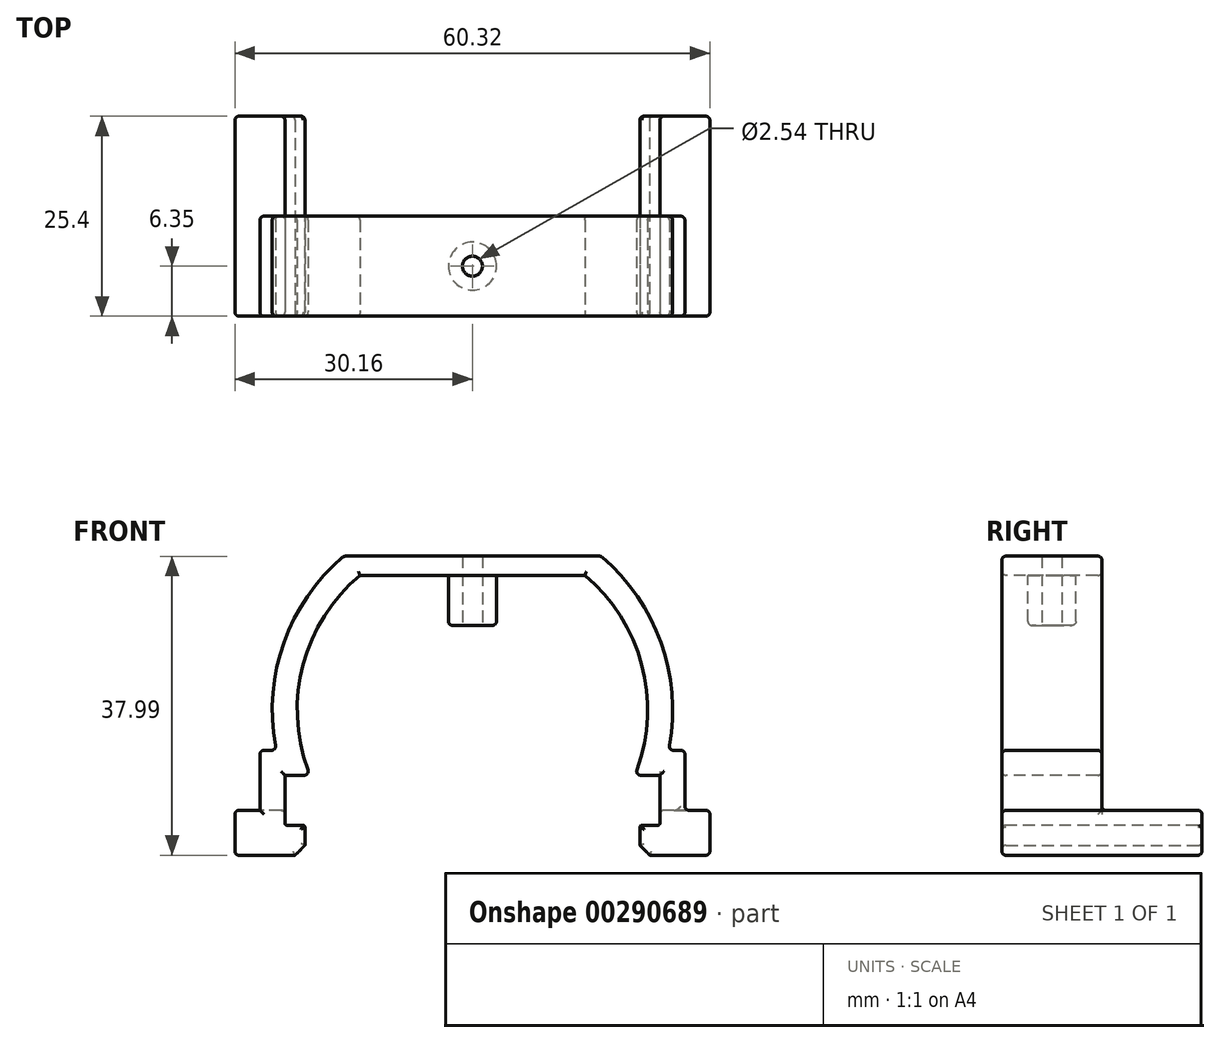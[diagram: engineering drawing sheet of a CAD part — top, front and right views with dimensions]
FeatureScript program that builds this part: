
annotation { "Feature Type Name" : "Feature", "Feature Type Description" : "" }
export const myFeature = defineFeature(function(context is Context, id is Id, definition is map)
    precondition{}
    {
        {
            var Q0;
            Q0=qCreatedBy(makeId("Front.planeOp"),FACE);
            var sketch = newSketch(context, id + "F0", { "sketchPlane" : qUnion([Q0])});
            skLineSegment(sketch, "E0", {"start": v(-23.81, 0) * mm, "end": v(-20.64, 0) * mm});
            skLineSegment(sketch, "E1", {"start": v(0, 0) * mm, "end": v(0, 25.4) * mm, "construction": true});
            skLineSegment(sketch, "E2", {"start": v(-14.29, 25.4) * mm, "end": v(14.29, 25.4) * mm});
            skLineSegment(sketch, "E3", {"start": v(-23.81, 0) * mm, "end": v(-20.64, 0) * mm, "construction": true});
            skLineSegment(sketch, "E4", {"start": v(23.81, 0) * mm, "end": v(20.64, 0) * mm, "construction": true});
            skArc(sketch, "E5", {"start": v(-14.29, 25.4) * mm, "mid": v(-21.6, 13.73) * mm, "end": v(-20.64, 0) * mm});
            skLineSegment(sketch, "E6", {"start": v(-23.81, 0) * mm, "end": v(-23.81, -6.35) * mm});
            skLineSegment(sketch, "E7", {"start": v(23.81, 0) * mm, "end": v(23.81, -6.35) * mm});
            skArc(sketch, "E8.0", {"start": v(-16.33, 27.83) * mm, "mid": v(-24.02, 16.69) * mm, "end": v(-24.9, 3.18) * mm});
            skLineSegment(sketch, "E9", {"start": v(-16.33, 27.83) * mm, "end": v(16.33, 27.83) * mm});
            skLineSegment(sketch, "E10", {"start": v(-26.99, -4.45) * mm, "end": v(-26.99, 3.17) * mm});
            skLineSegment(sketch, "E11", {"start": v(-26.99, 3.17) * mm, "end": v(-24.9, 3.17) * mm});
            skLineSegment(sketch, "E12", {"start": v(26.99, -4.45) * mm, "end": v(26.99, 3.18) * mm});
            skLineSegment(sketch, "E13", {"start": v(26.99, 3.18) * mm, "end": v(24.9, 3.18) * mm});
            skArc(sketch, "E14.trimOffspring", {"start": v(24.9, 3.18) * mm, "mid": v(24.02, 16.69) * mm, "end": v(16.33, 27.83) * mm});
            skArc(sketch, "E15.trimOffspring", {"start": v(20.64, 0) * mm, "mid": v(21.6, 13.73) * mm, "end": v(14.29, 25.4) * mm});
            skLineSegment(sketch, "E16.trimOffspring", {"start": v(20.64, 0) * mm, "end": v(23.81, 0) * mm});
            skLineSegment(sketch, "E17", {"start": v(-23.81, -6.35) * mm, "end": v(-21.27, -6.35) * mm});
            skLineSegment(sketch, "E18", {"start": v(23.81, -6.35) * mm, "end": v(21.27, -6.35) * mm});
            skLineSegment(sketch, "E19", {"start": v(-26.99, -4.45) * mm, "end": v(-30.16, -4.45) * mm});
            skLineSegment(sketch, "E20", {"start": v(26.99, -4.45) * mm, "end": v(30.16, -4.45) * mm});
            skLineSegment(sketch, "E21", {"start": v(-30.16, -4.45) * mm, "end": v(-30.16, -10.16) * mm});
            skLineSegment(sketch, "E22", {"start": v(30.16, -4.45) * mm, "end": v(30.16, -10.16) * mm});
            skLineSegment(sketch, "E23", {"start": v(-21.27, -6.35) * mm, "end": v(-21.27, -10.16) * mm});
            skLineSegment(sketch, "E24", {"start": v(21.27, -6.35) * mm, "end": v(21.27, -10.16) * mm});
            skLineSegment(sketch, "E25", {"start": v(-21.27, -10.16) * mm, "end": v(-30.16, -10.16) * mm});
            skLineSegment(sketch, "E26", {"start": v(21.27, -10.16) * mm, "end": v(30.16, -10.16) * mm});
            skSolve(sketch);
        }
        {
            var Q0;
            Q0=makeQuery(id+"F0.imprint","IMPRINT",FACE,{"disambiguationData":[TD([[makeQuery(id+"F0.imprint","IMPRINT",EDGE,{"derivedFrom":sQuery(id+"F0.wireOp",EDGE,"E0")}),1.0]])]});
            extrude(context, id + "F1", {"entities" : qUnion([Q0]), "oppositeDirection" : true, "depth" : 12.7 * mm});
        }
        {
            var Q0;
            Q0=makeQuery(id+"F1.opExtrude","SWEPT_FACE",FACE,{"disambiguationData":[OSD([sQuery(id+"F0.wireOp",EDGE,"E2")])]});
            var sketch = newSketch(context, id + "F2", { "sketchPlane" : qUnion([Q0])});
            skLineSegment(sketch, "E27", {"start": v(0, -12.7) * mm, "end": v(0, -6.35) * mm, "construction": true});
            skPoint(sketch, "E27.endSnap0", {"position": v(0, -12.7) * mm});
            skCircle(sketch, "E28", {"center": v(0, -6.35) * mm, "radius": 3.05 * mm});
            skSolve(sketch);
        }
        {
            var Q0;
            Q0=makeQuery(id+"F2.imprint","IMPRINT",FACE,{"disambiguationData":[TD([[makeQuery(id+"F2.imprint","IMPRINT",EDGE,{"derivedFrom":sQuery(id+"F2.wireOp",EDGE,"E28")}),1.0]])]});
            extrude(context, id + "F3", {"entities" : qUnion([Q0]), "operationType" : NewBodyOperationType.ADD, "depth" : 6.35 * mm});
        }
        {
            var Q0;
            Q0=makeQuery(id+"F1.opExtrude","SWEPT_EDGE",EDGE,{"disambiguationData":[OSD([sQuery(id+"F0.wireOp",EDGE,"E17"),sQuery(id+"F0.wireOp",EDGE,"sQ2Dt9HJ-DLmy-fobY-wEzB-knzwlTL04auf")])]});
            var Q1;
            Q1=makeQuery(id+"F1.opExtrude","SWEPT_EDGE",EDGE,{"disambiguationData":[OSD([sQuery(id+"F0.wireOp",EDGE,"E18"),sQuery(id+"F0.wireOp",EDGE,"bWk3n836-9KEs-FhVF-pOS5-eo05tRzIyBKB")])]});
            fillet(context, id + "F4", {"entities" : qUnion([Q0, Q1]), "radius" : 0.25 * mm, "tangentPropagation" : true, "allowEdgeOverflow" : false});
        }
        {
            var Q0;
            Q0=makeQuery(id+"F1.opExtrude","SWEPT_EDGE",EDGE,{"disambiguationData":[OSD([sQuery(id+"F0.wireOp",EDGE,"E24"),sQuery(id+"F0.wireOp",EDGE,"E26")])]});
            chamfer(context, id + "F5", {"entities" : qUnion([Q0]), "width" : 1.27 * mm, "tangentPropagation" : true});
        }
        {
            var Q0;
            Q0=makeQuery(id+"F1.opExtrude","CAP_FACE",FACE,{"disambiguationData":[OSD([sQuery(id+"F0.wireOp",EDGE,"E0"),sQuery(id+"F0.wireOp",EDGE,"E2"),sQuery(id+"F0.wireOp",EDGE,"E5"),sQuery(id+"F0.wireOp",EDGE,"E6"),sQuery(id+"F0.wireOp",EDGE,"E7"),sQuery(id+"F0.wireOp",EDGE,"E8.0"),sQuery(id+"F0.wireOp",EDGE,"E9"),sQuery(id+"F0.wireOp",EDGE,"E10"),sQuery(id+"F0.wireOp",EDGE,"E11"),sQuery(id+"F0.wireOp",EDGE,"E12"),sQuery(id+"F0.wireOp",EDGE,"E13"),sQuery(id+"F0.wireOp",EDGE,"E14.trimOffspring"),sQuery(id+"F0.wireOp",EDGE,"E15.trimOffspring"),sQuery(id+"F0.wireOp",EDGE,"E16.trimOffspring"),sQuery(id+"F0.wireOp",EDGE,"E17"),sQuery(id+"F0.wireOp",EDGE,"E18"),sQuery(id+"F0.wireOp",EDGE,"E19"),sQuery(id+"F0.wireOp",EDGE,"E20"),sQuery(id+"F0.wireOp",EDGE,"E21"),sQuery(id+"F0.wireOp",EDGE,"E22"),sQuery(id+"F0.wireOp",EDGE,"E23"),sQuery(id+"F0.wireOp",EDGE,"E24"),sQuery(id+"F0.wireOp",EDGE,"E25"),sQuery(id+"F0.wireOp",EDGE,"E26")])],"isStart":false});
            var sketch = newSketch(context, id + "F6", { "sketchPlane" : qUnion([Q0])});
            skLineSegment(sketch, "E29", {"start": v(-26.99, -4.45) * mm, "end": v(-23.81, -4.45) * mm});
            skSolve(sketch);
        }
        {
            var Q0;
            {var subQ3=sQuery(id+"F6.wireOp",EDGE,"E29");Q0=makeQuery(id+"F6.imprint","IMPRINT",FACE,{"disambiguationData":[TD([[makeQuery(id+"F6.imprint","IMPRINT",EDGE,{"derivedFrom":subQ3}),-1.0]])]});}
            extrude(context, id + "F7", {"entities" : qUnion([Q0]), "operationType" : NewBodyOperationType.ADD, "depth" : 12.7 * mm});
        }
        {
            var Q0;
            Q0=makeQuery(id+"F1.opExtrude","CAP_FACE",FACE,{"disambiguationData":[OSD([sQuery(id+"F0.wireOp",EDGE,"E0"),sQuery(id+"F0.wireOp",EDGE,"E2"),sQuery(id+"F0.wireOp",EDGE,"E5"),sQuery(id+"F0.wireOp",EDGE,"E6"),sQuery(id+"F0.wireOp",EDGE,"E7"),sQuery(id+"F0.wireOp",EDGE,"E8.0"),sQuery(id+"F0.wireOp",EDGE,"E9"),sQuery(id+"F0.wireOp",EDGE,"E10"),sQuery(id+"F0.wireOp",EDGE,"E11"),sQuery(id+"F0.wireOp",EDGE,"E12"),sQuery(id+"F0.wireOp",EDGE,"E13"),sQuery(id+"F0.wireOp",EDGE,"E14.trimOffspring"),sQuery(id+"F0.wireOp",EDGE,"E15.trimOffspring"),sQuery(id+"F0.wireOp",EDGE,"E16.trimOffspring"),sQuery(id+"F0.wireOp",EDGE,"E17"),sQuery(id+"F0.wireOp",EDGE,"E18"),sQuery(id+"F0.wireOp",EDGE,"E19"),sQuery(id+"F0.wireOp",EDGE,"E20"),sQuery(id+"F0.wireOp",EDGE,"E21"),sQuery(id+"F0.wireOp",EDGE,"E22"),sQuery(id+"F0.wireOp",EDGE,"E23"),sQuery(id+"F0.wireOp",EDGE,"E24"),sQuery(id+"F0.wireOp",EDGE,"E25"),sQuery(id+"F0.wireOp",EDGE,"E26")])],"isStart":false});
            var sketch = newSketch(context, id + "F8", { "sketchPlane" : qUnion([Q0])});
            skLineSegment(sketch, "E30", {"start": v(26.99, -4.45) * mm, "end": v(23.81, -4.45) * mm});
            skSolve(sketch);
        }
        {
            var Q0;
            {var subQ9=sQuery(id+"F8.wireOp",EDGE,"E30");Q0=makeQuery(id+"F8.imprint","IMPRINT",FACE,{"disambiguationData":[TD([[makeQuery(id+"F8.imprint","IMPRINT",EDGE,{"derivedFrom":subQ9}),1.0]])]});}
            extrude(context, id + "F9", {"entities" : qUnion([Q0]), "operationType" : NewBodyOperationType.ADD, "depth" : 12.7 * mm});
        }
        {
            var Q0;
            {var subQ0=sQuery(id+"F0.wireOp",EDGE,"E25");var subQ1=sQuery(id+"F0.wireOp",EDGE,"E23");Q0=makeQuery(id+"F9.boolean.opBoolean","MERGE",EDGE,{"derivedFrom":[makeQuery(id+"F1.opExtrude","SWEPT_EDGE",EDGE,{"disambiguationData":[OSD([subQ1,subQ0])]}),makeQuery(id+"F9.opExtrude","SWEPT_EDGE",EDGE,{"disambiguationData":[OSD([subQ1,subQ0])]})]});}
            chamfer(context, id + "F10", {"entities" : qUnion([Q0]), "width" : 1.27 * mm, "tangentPropagation" : true});
        }
        {
            var Q0;
            Q0=makeQuery(id+"F1.opExtrude","CAP_EDGE",EDGE,{"disambiguationData":[OSD([sQuery(id+"F0.wireOp",EDGE,"E5")])],"isStart":true});
            var Q1;
            Q1=makeQuery(id+"F1.opExtrude","SWEPT_EDGE",EDGE,{"disambiguationData":[OSD([sQuery(id+"F0.wireOp",EDGE,"E0"),sQuery(id+"F0.wireOp",EDGE,"E5")])]});
            var Q2;
            Q2=makeQuery(id+"F1.opExtrude","CAP_EDGE",EDGE,{"disambiguationData":[OSD([sQuery(id+"F0.wireOp",EDGE,"E5")])],"isStart":false});
            var Q3;
            Q3=makeQuery(id+"F1.opExtrude","SWEPT_EDGE",EDGE,{"disambiguationData":[OSD([sQuery(id+"F0.wireOp",EDGE,"E13"),sQuery(id+"F0.wireOp",EDGE,"E14.trimOffspring")])]});
            var Q4;
            Q4=makeQuery(id+"F1.opExtrude","CAP_EDGE",EDGE,{"disambiguationData":[OSD([sQuery(id+"F0.wireOp",EDGE,"E6")])],"isStart":true});
            var Q5;
            Q5=makeQuery(id+"F1.opExtrude","CAP_EDGE",EDGE,{"disambiguationData":[OSD([sQuery(id+"F0.wireOp",EDGE,"E0")])],"isStart":true});
            var Q6;
            Q6=makeQuery(id+"F1.opExtrude","CAP_EDGE",EDGE,{"disambiguationData":[OSD([sQuery(id+"F0.wireOp",EDGE,"E17")])],"isStart":true});
            var Q7;
            Q7=makeQuery(id+"F1.opExtrude","CAP_EDGE",EDGE,{"disambiguationData":[OSD([sQuery(id+"F0.wireOp",EDGE,"E22")])],"isStart":true});
            var Q8;
            Q8=makeQuery(id+"F1.opExtrude","CAP_EDGE",EDGE,{"disambiguationData":[OSD([sQuery(id+"F0.wireOp",EDGE,"E18")])],"isStart":true});
            var Q9;
            Q9=makeQuery(id+"F1.opExtrude","CAP_EDGE",EDGE,{"disambiguationData":[OSD([sQuery(id+"F0.wireOp",EDGE,"E12")])],"isStart":true});
            var Q10;
            Q10=makeQuery(id+"F1.opExtrude","CAP_EDGE",EDGE,{"disambiguationData":[OSD([sQuery(id+"F0.wireOp",EDGE,"E14.trimOffspring")])],"isStart":true});
            var Q11;
            Q11=makeQuery(id+"F1.opExtrude","CAP_EDGE",EDGE,{"disambiguationData":[OSD([sQuery(id+"F0.wireOp",EDGE,"E13")])],"isStart":true});
            var Q12;
            Q12=makeQuery(id+"F1.opExtrude","CAP_EDGE",EDGE,{"disambiguationData":[OSD([sQuery(id+"F0.wireOp",EDGE,"E13")])],"isStart":false});
            var Q13;
            Q13=makeQuery(id+"F1.opExtrude","CAP_EDGE",EDGE,{"disambiguationData":[OSD([sQuery(id+"F0.wireOp",EDGE,"E20")])],"isStart":true});
            var Q14;
            Q14=makeQuery(id+"F1.opExtrude","CAP_EDGE",EDGE,{"disambiguationData":[OSD([sQuery(id+"F0.wireOp",EDGE,"E16.trimOffspring")])],"isStart":false});
            var Q15;
            Q15=makeQuery(id+"F1.opExtrude","SWEPT_EDGE",EDGE,{"disambiguationData":[OSD([sQuery(id+"F0.wireOp",EDGE,"E15.trimOffspring"),sQuery(id+"F0.wireOp",EDGE,"E16.trimOffspring")])]});
            var Q16;
            Q16=makeQuery(id+"F1.opExtrude","CAP_EDGE",EDGE,{"disambiguationData":[OSD([sQuery(id+"F0.wireOp",EDGE,"E9")])],"isStart":false});
            var Q17;
            Q17=makeQuery(id+"F1.opExtrude","CAP_EDGE",EDGE,{"disambiguationData":[OSD([sQuery(id+"F0.wireOp",EDGE,"E2")])],"isStart":false});
            var Q18;
            Q18=makeQuery(id+"F1.opExtrude","CAP_EDGE",EDGE,{"disambiguationData":[OSD([sQuery(id+"F0.wireOp",EDGE,"E15.trimOffspring")])],"isStart":false});
            var Q19;
            Q19=makeQuery(id+"F1.opExtrude","CAP_EDGE",EDGE,{"disambiguationData":[OSD([sQuery(id+"F0.wireOp",EDGE,"E14.trimOffspring")])],"isStart":false});
            var Q20;
            Q20=makeQuery(id+"F1.opExtrude","SWEPT_EDGE",EDGE,{"disambiguationData":[OSD([sQuery(id+"F0.wireOp",EDGE,"E9"),sQuery(id+"F0.wireOp",EDGE,"E14.trimOffspring")])]});
            var Q21;
            Q21=makeQuery(id+"F1.opExtrude","SWEPT_EDGE",EDGE,{"disambiguationData":[OSD([sQuery(id+"F0.wireOp",EDGE,"E8.0"),sQuery(id+"F0.wireOp",EDGE,"E9")])]});
            var Q22;
            Q22=makeQuery(id+"F1.opExtrude","CAP_EDGE",EDGE,{"disambiguationData":[OSD([sQuery(id+"F0.wireOp",EDGE,"E9")])],"isStart":true});
            var Q23;
            Q23=makeQuery(id+"F1.opExtrude","CAP_EDGE",EDGE,{"disambiguationData":[OSD([sQuery(id+"F0.wireOp",EDGE,"E8.0")])],"isStart":true});
            var Q24;
            Q24=makeQuery(id+"F1.opExtrude","SWEPT_EDGE",EDGE,{"disambiguationData":[OSD([sQuery(id+"F0.wireOp",EDGE,"E8.0"),sQuery(id+"F0.wireOp",EDGE,"E11")])]});
            var Q25;
            Q25=makeQuery(id+"F1.opExtrude","CAP_EDGE",EDGE,{"disambiguationData":[OSD([sQuery(id+"F0.wireOp",EDGE,"E0")])],"isStart":false});
            var Q26;
            Q26=makeQuery(id+"F1.opExtrude","CAP_EDGE",EDGE,{"disambiguationData":[OSD([sQuery(id+"F0.wireOp",EDGE,"E8.0")])],"isStart":false});
            var Q27;
            Q27=makeQuery(id+"F1.opExtrude","CAP_EDGE",EDGE,{"disambiguationData":[OSD([sQuery(id+"F0.wireOp",EDGE,"E11")])],"isStart":false});
            var Q28;
            Q28=makeQuery(id+"F1.opExtrude","CAP_EDGE",EDGE,{"disambiguationData":[OSD([sQuery(id+"F0.wireOp",EDGE,"E10")])],"isStart":true});
            var Q29;
            Q29=makeQuery(id+"F1.opExtrude","CAP_EDGE",EDGE,{"disambiguationData":[OSD([sQuery(id+"F0.wireOp",EDGE,"E11")])],"isStart":true});
            var Q30;
            Q30=makeQuery(id+"F1.opExtrude","SWEPT_EDGE",EDGE,{"disambiguationData":[OSD([sQuery(id+"F0.wireOp",EDGE,"E19"),sQuery(id+"F0.wireOp",EDGE,"E21")])]});
            var Q31;
            Q31=makeQuery(id+"F1.opExtrude","CAP_EDGE",EDGE,{"disambiguationData":[OSD([sQuery(id+"F0.wireOp",EDGE,"E19")])],"isStart":true});
            var Q32;
            Q32=makeQuery(id+"F1.opExtrude","CAP_EDGE",EDGE,{"disambiguationData":[OSD([sQuery(id+"F0.wireOp",EDGE,"E21")])],"isStart":true});
            var Q33;
            Q33=makeQuery(id+"F1.opExtrude","SWEPT_EDGE",EDGE,{"disambiguationData":[OSD([sQuery(id+"F0.wireOp",EDGE,"E19"),sQuery(id+"F0.wireOp",EDGE,"E21")])]});
            var Q34;
            Q34=makeQuery(id+"F1.opExtrude","CAP_EDGE",EDGE,{"disambiguationData":[OSD([sQuery(id+"F0.wireOp",EDGE,"E2")])],"isStart":true});
            var Q35;
            Q35=makeQuery(id+"F1.opExtrude","CAP_EDGE",EDGE,{"disambiguationData":[OSD([sQuery(id+"F0.wireOp",EDGE,"E15.trimOffspring")])],"isStart":true});
            var Q36;
            Q36=makeQuery(id+"F1.opExtrude","CAP_EDGE",EDGE,{"disambiguationData":[OSD([sQuery(id+"F0.wireOp",EDGE,"E16.trimOffspring")])],"isStart":true});
            var Q37;
            Q37=makeQuery(id+"F1.opExtrude","CAP_EDGE",EDGE,{"disambiguationData":[OSD([sQuery(id+"F0.wireOp",EDGE,"E7")])],"isStart":true});
            var Q38;
            Q38=makeQuery(id+"F3.opExtrude","CAP_EDGE",EDGE,{"disambiguationData":[OSD([sQuery(id+"F2.wireOp",EDGE,"E28")])],"isStart":false});
            var Q39;
            Q39=makeQuery(id+"F1.opExtrude","SWEPT_EDGE",EDGE,{"disambiguationData":[OSD([sQuery(id+"F0.wireOp",EDGE,"E12"),sQuery(id+"F0.wireOp",EDGE,"E13")])]});
            var Q40;
            Q40=makeQuery(id+"F1.opExtrude","SWEPT_EDGE",EDGE,{"disambiguationData":[OSD([sQuery(id+"F0.wireOp",EDGE,"E10"),sQuery(id+"F0.wireOp",EDGE,"E11")])]});
            var Q41;
            Q41=makeQuery(id+"F1.opExtrude","SWEPT_EDGE",EDGE,{"disambiguationData":[OSD([sQuery(id+"F0.wireOp",EDGE,"E17"),sQuery(id+"F0.wireOp",EDGE,"E23")])]});
            var Q42;
            Q42=makeQuery(id+"F1.opExtrude","CAP_EDGE",EDGE,{"disambiguationData":[OSD([sQuery(id+"F0.wireOp",EDGE,"E25")])],"isStart":true});
            var Q43;
            Q43=makeQuery(id+"F1.opExtrude","CAP_EDGE",EDGE,{"disambiguationData":[OSD([sQuery(id+"F0.wireOp",EDGE,"E23")])],"isStart":true});
            var Q44;
            Q44=makeQuery(id+"F1.opExtrude","CAP_EDGE",EDGE,{"disambiguationData":[OSD([sQuery(id+"F0.wireOp",EDGE,"E24")])],"isStart":true});
            var Q45;
            Q45=makeQuery(id+"F1.opExtrude","CAP_EDGE",EDGE,{"disambiguationData":[OSD([sQuery(id+"F0.wireOp",EDGE,"E26")])],"isStart":true});
            var Q46;
            Q46=makeQuery(id+"F7.opExtrude","CAP_FACE",FACE,{"disambiguationData":[OSD([sQuery(id+"F0.wireOp",EDGE,"E0"),sQuery(id+"F0.wireOp",EDGE,"E2"),sQuery(id+"F0.wireOp",EDGE,"E5"),sQuery(id+"F0.wireOp",EDGE,"E6"),sQuery(id+"F0.wireOp",EDGE,"E7"),sQuery(id+"F0.wireOp",EDGE,"E8.0"),sQuery(id+"F0.wireOp",EDGE,"E9"),sQuery(id+"F0.wireOp",EDGE,"E10"),sQuery(id+"F0.wireOp",EDGE,"E11"),sQuery(id+"F0.wireOp",EDGE,"E12"),sQuery(id+"F0.wireOp",EDGE,"E13"),sQuery(id+"F0.wireOp",EDGE,"E14.trimOffspring"),sQuery(id+"F0.wireOp",EDGE,"E15.trimOffspring"),sQuery(id+"F0.wireOp",EDGE,"E16.trimOffspring"),sQuery(id+"F0.wireOp",EDGE,"E17"),sQuery(id+"F0.wireOp",EDGE,"E18"),sQuery(id+"F0.wireOp",EDGE,"E19"),sQuery(id+"F0.wireOp",EDGE,"E20"),sQuery(id+"F0.wireOp",EDGE,"E21"),sQuery(id+"F0.wireOp",EDGE,"E22"),sQuery(id+"F0.wireOp",EDGE,"E23"),sQuery(id+"F0.wireOp",EDGE,"E24"),sQuery(id+"F0.wireOp",EDGE,"E25"),sQuery(id+"F0.wireOp",EDGE,"E26"),sQuery(id+"F6.wireOp",EDGE,"E29")])],"isStart":false});
            var Q47;
            {var subQ0=sQuery(id+"F0.wireOp",EDGE,"E22");var subQ1=sQuery(id+"F0.wireOp",EDGE,"E20");Q47=makeQuery(id+"F7.boolean.opBoolean","MERGE",EDGE,{"derivedFrom":[makeQuery(id+"F1.opExtrude","SWEPT_EDGE",EDGE,{"disambiguationData":[OSD([subQ1,subQ0])]}),makeQuery(id+"F7.opExtrude","SWEPT_EDGE",EDGE,{"disambiguationData":[OSD([subQ1,subQ0])]})]});}
            var Q48;
            Q48=makeQuery(id+"F1.opExtrude","CAP_EDGE",EDGE,{"disambiguationData":[OSD([sQuery(id+"F0.wireOp",EDGE,"E12")])],"isStart":false});
            var Q49;
            Q49=makeQuery(id+"F1.opExtrude","SWEPT_EDGE",EDGE,{"disambiguationData":[OSD([sQuery(id+"F0.wireOp",EDGE,"E12"),sQuery(id+"F0.wireOp",EDGE,"E20")])]});
            var Q50;
            {var subQ0=sQuery(id+"F0.wireOp",EDGE,"E26");var subQ1=sQuery(id+"F0.wireOp",EDGE,"E22");Q50=makeQuery(id+"F7.boolean.opBoolean","MERGE",EDGE,{"derivedFrom":[makeQuery(id+"F1.opExtrude","SWEPT_EDGE",EDGE,{"disambiguationData":[OSD([subQ1,subQ0])]}),makeQuery(id+"F7.opExtrude","SWEPT_EDGE",EDGE,{"disambiguationData":[OSD([subQ1,subQ0])]})]});}
            var Q51;
            Q51=makeQuery(id+"F9.opExtrude","CAP_FACE",FACE,{"disambiguationData":[OSD([sQuery(id+"F0.wireOp",EDGE,"E0"),sQuery(id+"F0.wireOp",EDGE,"E2"),sQuery(id+"F0.wireOp",EDGE,"E5"),sQuery(id+"F0.wireOp",EDGE,"E6"),sQuery(id+"F0.wireOp",EDGE,"E7"),sQuery(id+"F0.wireOp",EDGE,"E8.0"),sQuery(id+"F0.wireOp",EDGE,"E9"),sQuery(id+"F0.wireOp",EDGE,"E10"),sQuery(id+"F0.wireOp",EDGE,"E11"),sQuery(id+"F0.wireOp",EDGE,"E12"),sQuery(id+"F0.wireOp",EDGE,"E13"),sQuery(id+"F0.wireOp",EDGE,"E14.trimOffspring"),sQuery(id+"F0.wireOp",EDGE,"E15.trimOffspring"),sQuery(id+"F0.wireOp",EDGE,"E16.trimOffspring"),sQuery(id+"F0.wireOp",EDGE,"E17"),sQuery(id+"F0.wireOp",EDGE,"E18"),sQuery(id+"F0.wireOp",EDGE,"E19"),sQuery(id+"F0.wireOp",EDGE,"E20"),sQuery(id+"F0.wireOp",EDGE,"E21"),sQuery(id+"F0.wireOp",EDGE,"E22"),sQuery(id+"F0.wireOp",EDGE,"E23"),sQuery(id+"F0.wireOp",EDGE,"E24"),sQuery(id+"F0.wireOp",EDGE,"E25"),sQuery(id+"F0.wireOp",EDGE,"E26"),sQuery(id+"F8.wireOp",EDGE,"E30")])],"isStart":false});
            var Q52;
            Q52=makeQuery(id+"F9.opExtrude","SWEPT_EDGE",EDGE,{"disambiguationData":[OSD([sQuery(id+"F0.wireOp",EDGE,"E6"),sQuery(id+"F8.wireOp",EDGE,"E30")])]});
            var Q53;
            Q53=makeQuery(id+"F1.opExtrude","CAP_EDGE",EDGE,{"disambiguationData":[OSD([sQuery(id+"F0.wireOp",EDGE,"E6")])],"isStart":false});
            var Q54;
            Q54=makeQuery(id+"F9.opExtrude","CAP_EDGE",EDGE,{"disambiguationData":[OSD([sQuery(id+"F0.wireOp",EDGE,"E19"),sQuery(id+"F8.wireOp",EDGE,"E30")])],"isStart":true});
            var Q55;
            Q55=makeQuery(id+"F1.opExtrude","CAP_EDGE",EDGE,{"disambiguationData":[OSD([sQuery(id+"F0.wireOp",EDGE,"E10")])],"isStart":false});
            var Q56;
            Q56=makeQuery(id+"F7.opExtrude","SWEPT_EDGE",EDGE,{"disambiguationData":[OSD([sQuery(id+"F0.wireOp",EDGE,"E7"),sQuery(id+"F6.wireOp",EDGE,"E29")])]});
            var Q57;
            {var subQ0=sQuery(id+"F0.wireOp",EDGE,"E25");var subQ1=sQuery(id+"F0.wireOp",EDGE,"E21");Q57=makeQuery(id+"F9.boolean.opBoolean","MERGE",EDGE,{"derivedFrom":[makeQuery(id+"F1.opExtrude","SWEPT_EDGE",EDGE,{"disambiguationData":[OSD([subQ1,subQ0])]}),makeQuery(id+"F9.opExtrude","SWEPT_EDGE",EDGE,{"disambiguationData":[OSD([subQ1,subQ0])]})]});}
            fillet(context, id + "F11", {"entities" : qUnion([Q0, Q1, Q2, Q3, Q4, Q5, Q6, Q7, Q8, Q9, Q10, Q11, Q12, Q13, Q14, Q15, Q16, Q17, Q18, Q19, Q20, Q21, Q22, Q23, Q24, Q25, Q26, Q27, Q28, Q29, Q30, Q31, Q32, Q33, Q34, Q35, Q36, Q37, Q38, Q39, Q40, Q41, Q42, Q43, Q44, Q45, Q46, Q47, Q48, Q49, Q50, Q51, Q52, Q53, Q54, Q55, Q56, Q57]), "radius" : 0.5 * mm, "tangentPropagation" : true, "allowEdgeOverflow" : false});
        }
        {
            var Q0;
            Q0=makeQuery(id+"F3.opExtrude","CAP_FACE",FACE,{"disambiguationData":[OSD([sQuery(id+"F2.wireOp",EDGE,"E28")])],"isStart":false});
            var sketch = newSketch(context, id + "F12", { "sketchPlane" : qUnion([Q0])});
            skCircle(sketch, "E31", {"center": v(0, -6.35) * mm, "radius": 1.27 * mm});
            skSolve(sketch);
        }
        {
            var Q0;
            Q0=makeQuery(id+"F12.imprint","IMPRINT",FACE,{"disambiguationData":[TD([[makeQuery(id+"F12.imprint","IMPRINT",EDGE,{"derivedFrom":sQuery(id+"F12.wireOp",EDGE,"E31")}),1.0]])]});
            extrude(context, id + "F13", {"entities" : qUnion([Q0]), "operationType" : NewBodyOperationType.REMOVE, "endBound" : BoundingType.UP_TO_NEXT, "oppositeDirection" : true, "depth" : 25.4 * mm});
        }
    });
